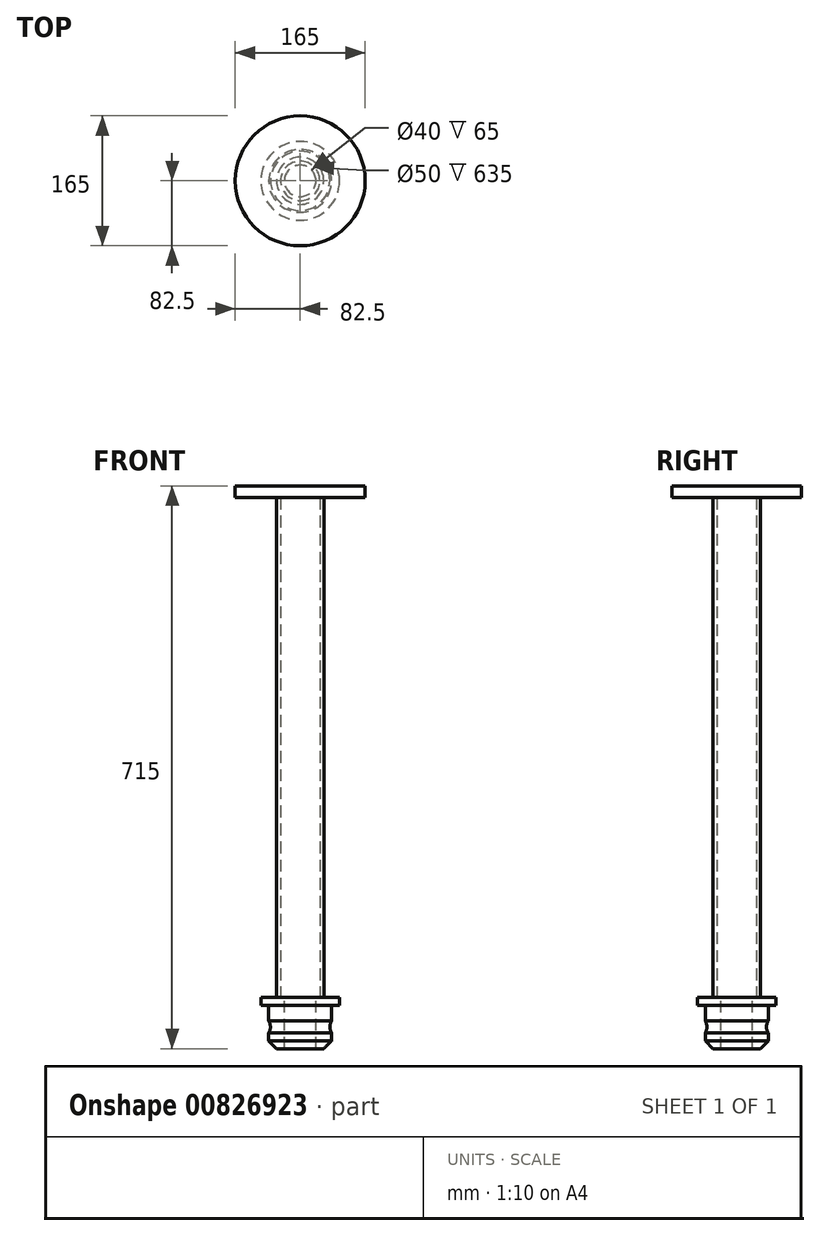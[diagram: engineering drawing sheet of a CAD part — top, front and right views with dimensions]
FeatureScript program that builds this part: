
annotation { "Feature Type Name" : "Feature", "Feature Type Description" : "" }
export const myFeature = defineFeature(function(context is Context, id is Id, definition is map)
    precondition{}
    {
        {
            var Q0;
            Q0=qCreatedBy(makeId("Right.planeOp"),FACE);
            var sketch = newSketch(context, id + "F0", { "sketchPlane" : qUnion([Q0])});
            skLineSegment(sketch, "E0", {"start": v(0, 0) * mm, "end": v(0, -50) * mm});
            skPoint(sketch, "E1.visualSharp", {"position": v(0, -650) * mm});
            skLineSegment(sketch, "E2", {"start": v(0, -50) * mm, "end": v(0, -650) * mm});
            skSolve(sketch);
        }
        {
            var Q0;
            Q0=qCreatedBy(makeId("Top.planeOp"),FACE);
            var sketch = newSketch(context, id + "F1", { "sketchPlane" : qUnion([Q0])});
            skCircle(sketch, "E3", {"center": v(0, 0) * mm, "radius": 25 * mm});
            skCircle(sketch, "E4", {"center": v(0, 0) * mm, "radius": 30 * mm});
            skSolve(sketch);
        }
        {
            var Q0;
            Q0=makeQuery(id+"F1.imprint","IMPRINT",FACE,{"disambiguationData":[TD([[makeQuery(id+"F1.imprint","IMPRINT",EDGE,{"derivedFrom":sQuery(id+"F1.wireOp",EDGE,"E3")}),-1.0]])]});
            var Q1;
            Q1=sQuery(id+"F0.wireOp",EDGE,"E0");
            var Q2;
            Q2=sQuery(id+"F0.wireOp",EDGE,"E2");
            sweep(context, id + "F2", {"profiles" : qUnion([Q0]), "path" : qUnion([Q1, Q2])});
        }
        {
            var Q0;
            Q0=qCreatedBy(makeId("Top.planeOp"),FACE);
            var sketch = newSketch(context, id + "F3", { "sketchPlane" : qUnion([Q0])});
            skCircle(sketch, "E5", {"center": v(0, 0) * mm, "radius": 82.5 * mm});
            skSolve(sketch);
        }
        {
            var Q0;
            Q0=makeQuery(id+"F3.imprint","IMPRINT",FACE,{"disambiguationData":[TD([[makeQuery(id+"F3.imprint","IMPRINT",EDGE,{"derivedFrom":sQuery(id+"F3.wireOp",EDGE,"E5")}),1.0]])]});
            extrude(context, id + "F4", {"entities" : qUnion([Q0]), "operationType" : NewBodyOperationType.ADD, "oppositeDirection" : true, "depth" : 15 * mm, "offsetDistance" : 25 * mm});
        }
        {
            var Q0;
            Q0=qCreatedBy(makeId("Front.planeOp"),FACE);
            var sketch = newSketch(context, id + "F5", { "sketchPlane" : qUnion([Q0])});
            skPoint(sketch, "E6.end.orphan", {"position": v(35, -650) * mm});
            skPoint(sketch, "E7.0.end.orphan", {"position": v(-30, -650) * mm});
            skPoint(sketch, "E7.0.start.orphan", {"position": v(30, -650) * mm});
            skLineSegment(sketch, "E8", {"start": v(35, -650) * mm, "end": v(50, -650) * mm});
            skLineSegment(sketch, "E9", {"start": v(50, -650) * mm, "end": v(50, -660) * mm});
            skLineSegment(sketch, "E10", {"start": v(30, -715) * mm, "end": v(20, -715) * mm});
            skLineSegment(sketch, "E11", {"start": v(20, -715) * mm, "end": v(20, -606.43) * mm});
            skLineSegment(sketch, "E12.0", {"start": v(30, -650) * mm, "end": v(-30, -650) * mm});
            skLineSegment(sketch, "E13", {"start": v(20, -650) * mm, "end": v(20, -606.43) * mm});
            skLineSegment(sketch, "E14", {"start": v(20, -650) * mm, "end": v(35, -650) * mm});
            skLineSegment(sketch, "E15", {"start": v(50, -660) * mm, "end": v(40, -660) * mm});
            skLineSegment(sketch, "E16", {"start": v(40, -660) * mm, "end": v(40, -680) * mm});
            skArc(sketch, "E17", {"start": v(40, -680) * mm, "mid": v(37.84, -687.5) * mm, "end": v(40, -695) * mm});
            skLineSegment(sketch, "E18", {"start": v(40, -695) * mm, "end": v(40, -705) * mm});
            skLineSegment(sketch, "E19", {"start": v(40, -705) * mm, "end": v(30, -715) * mm});
            skLineSegment(sketch, "E20", {"start": v(30, -15) * mm, "end": v(30, -600) * mm});
            skSolve(sketch);
        }
        {
            var Q0;
            {var subQ1=sQuery(id+"F5.wireOp",EDGE,"E8");Q0=makeQuery(id+"F5.imprint","IMPRINT",FACE,{"disambiguationData":[TD([[makeQuery(id+"F5.imprint","IMPRINT",EDGE,{"derivedFrom":subQ1}),-1.0]])]});}
            var Q1;
            Q1=makeQuery(id+"F2.opSweep","SWEPT_FACE",FACE,{"disambiguationData":[OSD([sQuery(id+"F0.wireOp",EDGE,"E0"),sQuery(id+"F1.wireOp",EDGE,"E4")])]});
            revolve(context, id + "F6", {"operationType" : NewBodyOperationType.ADD, "surfaceOperationType" : NewSurfaceOperationType.NEW, "entities" : qUnion([Q0]), "axis" : qUnion([Q1]), "revolveType" : RevolveType.FULL});
        }
    });
